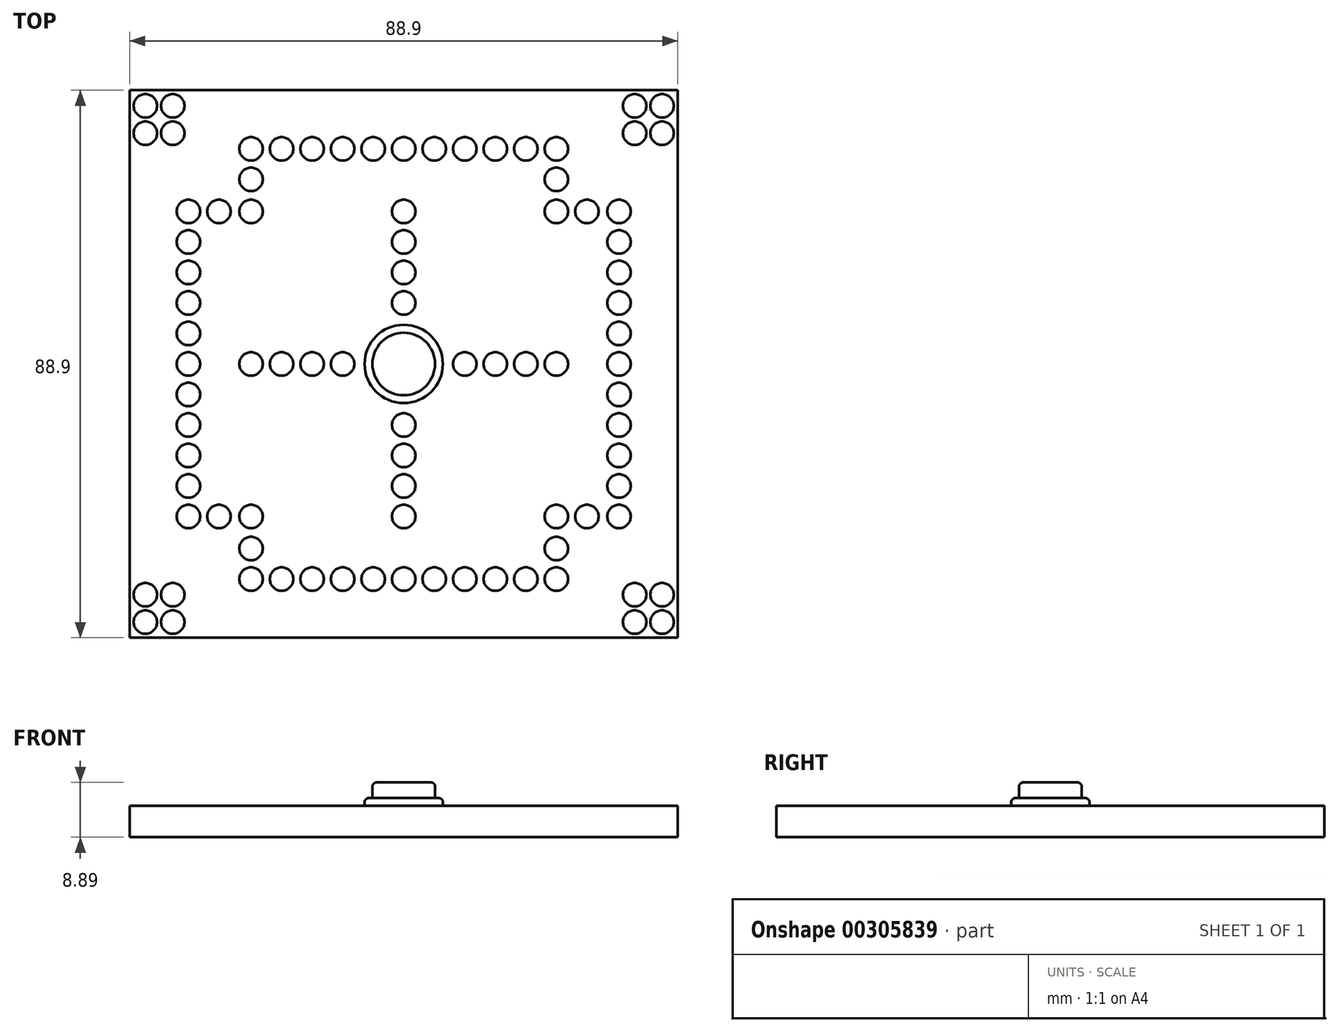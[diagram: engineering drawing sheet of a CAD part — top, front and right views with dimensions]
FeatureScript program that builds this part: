
annotation { "Feature Type Name" : "Feature", "Feature Type Description" : "" }
export const myFeature = defineFeature(function(context is Context, id is Id, definition is map)
    precondition{}
    {
        {
            var Q0;
            Q0=qCreatedBy(makeId("Top.planeOp"),FACE);
            var sketch = newSketch(context, id + "F0", { "sketchPlane" : qUnion([Q0])});
            skLineSegment(sketch, "E0.bottom", {"start": v(-44.45, 44.45) * mm, "end": v(44.45, 44.45) * mm});
            skLineSegment(sketch, "E0.top", {"start": v(-44.45, -44.45) * mm, "end": v(44.45, -44.45) * mm});
            skLineSegment(sketch, "E0.left", {"start": v(-44.45, 44.45) * mm, "end": v(-44.45, -44.45) * mm});
            skLineSegment(sketch, "E0.right", {"start": v(44.45, 44.45) * mm, "end": v(44.45, -44.45) * mm});
            skSolve(sketch);
        }
        {
            var Q0;
            Q0=makeQuery(id+"F0.imprint","IMPRINT",FACE,{"disambiguationData":[TD([[makeQuery(id+"F0.imprint","IMPRINT",EDGE,{"derivedFrom":sQuery(id+"F0.wireOp",EDGE,"E0.bottom")}),-1.0]])]});
            extrude(context, id + "F1", {"entities" : qUnion([Q0]), "depth" : 5.08 * mm});
        }
        {
            var Q0;
            Q0=makeQuery(id+"F1.opExtrude","CAP_FACE",FACE,{"disambiguationData":[OSD([sQuery(id+"F0.wireOp",EDGE,"E0.bottom"),sQuery(id+"F0.wireOp",EDGE,"E0.top"),sQuery(id+"F0.wireOp",EDGE,"E0.left"),sQuery(id+"F0.wireOp",EDGE,"E0.right")])],"isStart":false});
            var sketch = newSketch(context, id + "F2", { "sketchPlane" : qUnion([Q0])});
            skCircle(sketch, "E1", {"center": v(0, 24.77) * mm, "radius": 1.9 * mm});
            skCircle(sketch, "E2", {"center": v(24.77, 0) * mm, "radius": 1.9 * mm});
            skCircle(sketch, "E3", {"center": v(0, -24.77) * mm, "radius": 1.9 * mm});
            skCircle(sketch, "E4", {"center": v(-24.77, 0) * mm, "radius": 1.9 * mm});
            skCircle(sketch, "E5", {"center": v(0, 34.93) * mm, "radius": 1.9 * mm});
            skCircle(sketch, "E6", {"center": v(-24.77, 34.92) * mm, "radius": 1.9 * mm});
            skCircle(sketch, "E7.1.0.0", {"center": v(-19.81, 34.92) * mm, "radius": 1.9 * mm});
            skCircle(sketch, "E7.2.0.0", {"center": v(-14.86, 34.92) * mm, "radius": 1.9 * mm});
            skLineSegment(sketch, "E7.direction1", {"start": v(-24.77, 34.92) * mm, "end": v(-19.81, 34.92) * mm, "construction": true});
            skCircle(sketch, "E8.0.3.0", {"center": v(-9.9, 34.92) * mm, "radius": 1.9 * mm});
            skCircle(sketch, "E8.0.4.0", {"center": v(-4.95, 34.92) * mm, "radius": 1.9 * mm});
            skCircle(sketch, "E9.1.0.0", {"center": v(4.95, 34.93) * mm, "radius": 1.9 * mm});
            skCircle(sketch, "E9.2.0.0", {"center": v(9.9, 34.93) * mm, "radius": 1.9 * mm});
            skCircle(sketch, "E9.3.0.0", {"center": v(14.86, 34.93) * mm, "radius": 1.9 * mm});
            skCircle(sketch, "E9.4.0.0", {"center": v(19.81, 34.93) * mm, "radius": 1.9 * mm});
            skCircle(sketch, "E9.5.0.0", {"center": v(24.77, 34.93) * mm, "radius": 1.9 * mm});
            skLineSegment(sketch, "E9.direction1", {"start": v(0, 34.93) * mm, "end": v(4.95, 34.93) * mm, "construction": true});
            skCircle(sketch, "E10", {"center": v(24.77, 29.97) * mm, "radius": 1.9 * mm});
            skCircle(sketch, "E11", {"center": v(24.77, 24.77) * mm, "radius": 1.9 * mm});
            skCircle(sketch, "E12", {"center": v(-24.77, 24.76) * mm, "radius": 1.9 * mm});
            skCircle(sketch, "E13", {"center": v(-24.77, 29.97) * mm, "radius": 1.9 * mm});
            skCircle(sketch, "E14", {"center": v(24.77, -34.93) * mm, "radius": 1.9 * mm});
            skCircle(sketch, "E15.1.0.0", {"center": v(19.81, -34.93) * mm, "radius": 1.9 * mm});
            skCircle(sketch, "E15.2.0.0", {"center": v(14.86, -34.93) * mm, "radius": 1.9 * mm});
            skCircle(sketch, "E15.3.0.0", {"center": v(9.9, -34.93) * mm, "radius": 1.9 * mm});
            skCircle(sketch, "E15.4.0.0", {"center": v(4.95, -34.93) * mm, "radius": 1.9 * mm});
            skCircle(sketch, "E15.5.0.0", {"center": v(0, -34.93) * mm, "radius": 1.9 * mm});
            skCircle(sketch, "E15.6.0.0", {"center": v(-4.95, -34.93) * mm, "radius": 1.9 * mm});
            skCircle(sketch, "E15.7.0.0", {"center": v(-9.9, -34.93) * mm, "radius": 1.9 * mm});
            skCircle(sketch, "E15.8.0.0", {"center": v(-14.86, -34.93) * mm, "radius": 1.9 * mm});
            skCircle(sketch, "E15.9.0.0", {"center": v(-19.81, -34.93) * mm, "radius": 1.9 * mm});
            skCircle(sketch, "E15.10.0.0", {"center": v(-24.77, -34.93) * mm, "radius": 1.9 * mm});
            skLineSegment(sketch, "E15.direction1", {"start": v(24.77, -34.93) * mm, "end": v(19.81, -34.93) * mm, "construction": true});
            skCircle(sketch, "E16", {"center": v(-24.77, -24.77) * mm, "radius": 1.9 * mm});
            skCircle(sketch, "E17", {"center": v(24.77, -24.77) * mm, "radius": 1.9 * mm});
            skCircle(sketch, "E18", {"center": v(-24.76, -29.97) * mm, "radius": 1.9 * mm});
            skCircle(sketch, "E19", {"center": v(24.77, -29.97) * mm, "radius": 1.9 * mm});
            skCircle(sketch, "E20", {"center": v(-34.92, -24.77) * mm, "radius": 1.9 * mm});
            skCircle(sketch, "E21.0.1.0", {"center": v(-34.92, -19.81) * mm, "radius": 1.9 * mm});
            skCircle(sketch, "E21.0.2.0", {"center": v(-34.92, -14.86) * mm, "radius": 1.9 * mm});
            skCircle(sketch, "E21.0.3.0", {"center": v(-34.92, -9.9) * mm, "radius": 1.9 * mm});
            skCircle(sketch, "E21.0.4.0", {"center": v(-34.92, -4.95) * mm, "radius": 1.9 * mm});
            skCircle(sketch, "E21.0.5.0", {"center": v(-34.92, 0) * mm, "radius": 1.9 * mm});
            skCircle(sketch, "E21.0.6.0", {"center": v(-34.92, 4.95) * mm, "radius": 1.9 * mm});
            skCircle(sketch, "E21.0.7.0", {"center": v(-34.92, 9.9) * mm, "radius": 1.9 * mm});
            skCircle(sketch, "E21.0.8.0", {"center": v(-34.92, 14.86) * mm, "radius": 1.9 * mm});
            skCircle(sketch, "E21.0.9.0", {"center": v(-34.92, 19.81) * mm, "radius": 1.9 * mm});
            skCircle(sketch, "E21.0.10.0", {"center": v(-34.92, 24.77) * mm, "radius": 1.9 * mm});
            skLineSegment(sketch, "E21.direction2", {"start": v(-34.92, -24.77) * mm, "end": v(-34.92, -19.81) * mm, "construction": true});
            skCircle(sketch, "E22", {"center": v(34.93, -24.77) * mm, "radius": 1.9 * mm});
            skCircle(sketch, "E23", {"center": v(29.72, -24.77) * mm, "radius": 1.9 * mm});
            skCircle(sketch, "E24", {"center": v(29.72, 24.77) * mm, "radius": 1.9 * mm});
            skCircle(sketch, "E25", {"center": v(-29.97, -24.77) * mm, "radius": 1.9 * mm});
            skCircle(sketch, "E26", {"center": v(-29.97, 24.76) * mm, "radius": 1.9 * mm});
            skCircle(sketch, "E27.0.1.0", {"center": v(34.93, -19.81) * mm, "radius": 1.9 * mm});
            skCircle(sketch, "E27.0.2.0", {"center": v(34.93, -14.86) * mm, "radius": 1.9 * mm});
            skCircle(sketch, "E27.0.3.0", {"center": v(34.93, -9.9) * mm, "radius": 1.9 * mm});
            skCircle(sketch, "E27.0.4.0", {"center": v(34.93, -4.95) * mm, "radius": 1.9 * mm});
            skCircle(sketch, "E27.0.5.0", {"center": v(34.93, 0) * mm, "radius": 1.9 * mm});
            skCircle(sketch, "E27.0.6.0", {"center": v(34.93, 4.95) * mm, "radius": 1.9 * mm});
            skCircle(sketch, "E27.0.7.0", {"center": v(34.93, 9.9) * mm, "radius": 1.9 * mm});
            skCircle(sketch, "E27.0.8.0", {"center": v(34.93, 14.86) * mm, "radius": 1.9 * mm});
            skCircle(sketch, "E27.0.9.0", {"center": v(34.93, 19.81) * mm, "radius": 1.9 * mm});
            skCircle(sketch, "E27.0.10.0", {"center": v(34.93, 24.77) * mm, "radius": 1.9 * mm});
            skLineSegment(sketch, "E27.direction1", {"start": v(34.93, -24.77) * mm, "end": v(60.33, -24.77) * mm, "construction": true});
            skLineSegment(sketch, "E27.direction2", {"start": v(34.93, -24.77) * mm, "end": v(34.93, -19.81) * mm, "construction": true});
            skCircle(sketch, "E28.1.0.0", {"center": v(-19.81, 0) * mm, "radius": 1.9 * mm});
            skCircle(sketch, "E28.2.0.0", {"center": v(-14.86, 0) * mm, "radius": 1.9 * mm});
            skCircle(sketch, "E28.3.0.0", {"center": v(-9.9, 0) * mm, "radius": 1.9 * mm});
            skLineSegment(sketch, "E28.direction1", {"start": v(-24.77, 0) * mm, "end": v(-19.81, 0) * mm, "construction": true});
            skCircle(sketch, "E29.0.1.0", {"center": v(0, -19.81) * mm, "radius": 1.9 * mm});
            skCircle(sketch, "E29.2.0.0", {"center": v(50.8, -24.77) * mm, "radius": 1.9 * mm});
            skCircle(sketch, "E29.2.1.0", {"center": v(50.8, -19.81) * mm, "radius": 1.9 * mm});
            skLineSegment(sketch, "E29.direction2", {"start": v(0, -24.77) * mm, "end": v(0, -19.81) * mm, "construction": true});
            skCircle(sketch, "E30.0.0.2", {"center": v(0, -14.86) * mm, "radius": 1.9 * mm});
            skCircle(sketch, "E30.0.0.3", {"center": v(0, -9.9) * mm, "radius": 1.9 * mm});
            skCircle(sketch, "E30.0.2.2", {"center": v(50.8, -14.86) * mm, "radius": 1.9 * mm});
            skCircle(sketch, "E30.0.2.3", {"center": v(50.8, -9.9) * mm, "radius": 1.9 * mm});
            skCircle(sketch, "E31.0.1.0", {"center": v(0, 19.81) * mm, "radius": 1.9 * mm});
            skCircle(sketch, "E31.2.0.0", {"center": v(50.8, 24.77) * mm, "radius": 1.9 * mm});
            skCircle(sketch, "E31.2.1.0", {"center": v(50.8, 19.81) * mm, "radius": 1.9 * mm});
            skLineSegment(sketch, "E31.direction2", {"start": v(0, 24.77) * mm, "end": v(0, 19.81) * mm, "construction": true});
            skCircle(sketch, "E32.0.0.2", {"center": v(0, 14.86) * mm, "radius": 1.9 * mm});
            skCircle(sketch, "E32.0.0.3", {"center": v(0, 9.9) * mm, "radius": 1.9 * mm});
            skCircle(sketch, "E32.0.2.2", {"center": v(50.8, 14.86) * mm, "radius": 1.9 * mm});
            skCircle(sketch, "E32.0.2.3", {"center": v(50.8, 9.9) * mm, "radius": 1.9 * mm});
            skCircle(sketch, "E33.1.0.0", {"center": v(19.81, 0) * mm, "radius": 1.9 * mm});
            skCircle(sketch, "E33.2.0.0", {"center": v(14.86, 0) * mm, "radius": 1.9 * mm});
            skCircle(sketch, "E33.3.0.0", {"center": v(9.9, 0) * mm, "radius": 1.9 * mm});
            skLineSegment(sketch, "E33.direction1", {"start": v(24.77, 0) * mm, "end": v(19.81, 0) * mm, "construction": true});
            skSolve(sketch);
        }
        {
            var Q0;
            Q0=makeQuery(id+"F2.imprint","IMPRINT",FACE,{"disambiguationData":[TD([[makeQuery(id+"F2.imprint","IMPRINT",EDGE,{"derivedFrom":sQuery(id+"F2.wireOp",EDGE,"E20")}),1.0]])]});
            var Q1;
            Q1=makeQuery(id+"F2.imprint","IMPRINT",FACE,{"disambiguationData":[TD([[makeQuery(id+"F2.imprint","IMPRINT",EDGE,{"derivedFrom":sQuery(id+"F2.wireOp",EDGE,"E25")}),1.0]])]});
            var Q2;
            Q2=makeQuery(id+"F2.imprint","IMPRINT",FACE,{"disambiguationData":[TD([[makeQuery(id+"F2.imprint","IMPRINT",EDGE,{"derivedFrom":sQuery(id+"F2.wireOp",EDGE,"E16")}),1.0]])]});
            var Q3;
            Q3=makeQuery(id+"F2.imprint","IMPRINT",FACE,{"disambiguationData":[TD([[makeQuery(id+"F2.imprint","IMPRINT",EDGE,{"derivedFrom":sQuery(id+"F2.wireOp",EDGE,"E18")}),1.0]])]});
            var Q4;
            Q4=makeQuery(id+"F2.imprint","IMPRINT",FACE,{"disambiguationData":[TD([[makeQuery(id+"F2.imprint","IMPRINT",EDGE,{"derivedFrom":sQuery(id+"F2.wireOp",EDGE,"E15.10.0.0")}),1.0]])]});
            var Q5;
            Q5=makeQuery(id+"F2.imprint","IMPRINT",FACE,{"disambiguationData":[TD([[makeQuery(id+"F2.imprint","IMPRINT",EDGE,{"derivedFrom":sQuery(id+"F2.wireOp",EDGE,"E15.9.0.0")}),1.0]])]});
            var Q6;
            Q6=makeQuery(id+"F2.imprint","IMPRINT",FACE,{"disambiguationData":[TD([[makeQuery(id+"F2.imprint","IMPRINT",EDGE,{"derivedFrom":sQuery(id+"F2.wireOp",EDGE,"E15.8.0.0")}),1.0]])]});
            var Q7;
            Q7=makeQuery(id+"F2.imprint","IMPRINT",FACE,{"disambiguationData":[TD([[makeQuery(id+"F2.imprint","IMPRINT",EDGE,{"derivedFrom":sQuery(id+"F2.wireOp",EDGE,"E15.7.0.0")}),1.0]])]});
            var Q8;
            Q8=makeQuery(id+"F2.imprint","IMPRINT",FACE,{"disambiguationData":[TD([[makeQuery(id+"F2.imprint","IMPRINT",EDGE,{"derivedFrom":sQuery(id+"F2.wireOp",EDGE,"E15.6.0.0")}),1.0]])]});
            var Q9;
            Q9=makeQuery(id+"F2.imprint","IMPRINT",FACE,{"disambiguationData":[TD([[makeQuery(id+"F2.imprint","IMPRINT",EDGE,{"derivedFrom":sQuery(id+"F2.wireOp",EDGE,"E15.5.0.0")}),1.0]])]});
            var Q10;
            Q10=makeQuery(id+"F2.imprint","IMPRINT",FACE,{"disambiguationData":[TD([[makeQuery(id+"F2.imprint","IMPRINT",EDGE,{"derivedFrom":sQuery(id+"F2.wireOp",EDGE,"E15.4.0.0")}),1.0]])]});
            var Q11;
            Q11=makeQuery(id+"F2.imprint","IMPRINT",FACE,{"disambiguationData":[TD([[makeQuery(id+"F2.imprint","IMPRINT",EDGE,{"derivedFrom":sQuery(id+"F2.wireOp",EDGE,"E15.3.0.0")}),1.0]])]});
            var Q12;
            Q12=makeQuery(id+"F2.imprint","IMPRINT",FACE,{"disambiguationData":[TD([[makeQuery(id+"F2.imprint","IMPRINT",EDGE,{"derivedFrom":sQuery(id+"F2.wireOp",EDGE,"E15.2.0.0")}),1.0]])]});
            var Q13;
            Q13=makeQuery(id+"F2.imprint","IMPRINT",FACE,{"disambiguationData":[TD([[makeQuery(id+"F2.imprint","IMPRINT",EDGE,{"derivedFrom":sQuery(id+"F2.wireOp",EDGE,"E15.1.0.0")}),1.0]])]});
            var Q14;
            Q14=makeQuery(id+"F2.imprint","IMPRINT",FACE,{"disambiguationData":[TD([[makeQuery(id+"F2.imprint","IMPRINT",EDGE,{"derivedFrom":sQuery(id+"F2.wireOp",EDGE,"E14")}),1.0]])]});
            var Q15;
            Q15=makeQuery(id+"F2.imprint","IMPRINT",FACE,{"disambiguationData":[TD([[makeQuery(id+"F2.imprint","IMPRINT",EDGE,{"derivedFrom":sQuery(id+"F2.wireOp",EDGE,"E19")}),1.0]])]});
            var Q16;
            Q16=makeQuery(id+"F2.imprint","IMPRINT",FACE,{"disambiguationData":[TD([[makeQuery(id+"F2.imprint","IMPRINT",EDGE,{"derivedFrom":sQuery(id+"F2.wireOp",EDGE,"E17")}),1.0]])]});
            var Q17;
            Q17=makeQuery(id+"F2.imprint","IMPRINT",FACE,{"disambiguationData":[TD([[makeQuery(id+"F2.imprint","IMPRINT",EDGE,{"derivedFrom":sQuery(id+"F2.wireOp",EDGE,"E23")}),1.0]])]});
            var Q18;
            Q18=makeQuery(id+"F2.imprint","IMPRINT",FACE,{"disambiguationData":[TD([[makeQuery(id+"F2.imprint","IMPRINT",EDGE,{"derivedFrom":sQuery(id+"F2.wireOp",EDGE,"E22")}),1.0]])]});
            var Q19;
            Q19=makeQuery(id+"F2.imprint","IMPRINT",FACE,{"disambiguationData":[TD([[makeQuery(id+"F2.imprint","IMPRINT",EDGE,{"derivedFrom":sQuery(id+"F2.wireOp",EDGE,"E27.0.1.0")}),1.0]])]});
            var Q20;
            Q20=makeQuery(id+"F2.imprint","IMPRINT",FACE,{"disambiguationData":[TD([[makeQuery(id+"F2.imprint","IMPRINT",EDGE,{"derivedFrom":sQuery(id+"F2.wireOp",EDGE,"E27.0.2.0")}),1.0]])]});
            var Q21;
            Q21=makeQuery(id+"F2.imprint","IMPRINT",FACE,{"disambiguationData":[TD([[makeQuery(id+"F2.imprint","IMPRINT",EDGE,{"derivedFrom":sQuery(id+"F2.wireOp",EDGE,"E27.0.3.0")}),1.0]])]});
            var Q22;
            Q22=makeQuery(id+"F2.imprint","IMPRINT",FACE,{"disambiguationData":[TD([[makeQuery(id+"F2.imprint","IMPRINT",EDGE,{"derivedFrom":sQuery(id+"F2.wireOp",EDGE,"E27.0.4.0")}),1.0]])]});
            var Q23;
            Q23=makeQuery(id+"F2.imprint","IMPRINT",FACE,{"disambiguationData":[TD([[makeQuery(id+"F2.imprint","IMPRINT",EDGE,{"derivedFrom":sQuery(id+"F2.wireOp",EDGE,"E27.0.5.0")}),1.0]])]});
            var Q24;
            Q24=makeQuery(id+"F2.imprint","IMPRINT",FACE,{"disambiguationData":[TD([[makeQuery(id+"F2.imprint","IMPRINT",EDGE,{"derivedFrom":sQuery(id+"F2.wireOp",EDGE,"E27.0.6.0")}),1.0]])]});
            var Q25;
            Q25=makeQuery(id+"F2.imprint","IMPRINT",FACE,{"disambiguationData":[TD([[makeQuery(id+"F2.imprint","IMPRINT",EDGE,{"derivedFrom":sQuery(id+"F2.wireOp",EDGE,"E27.0.7.0")}),1.0]])]});
            var Q26;
            Q26=makeQuery(id+"F2.imprint","IMPRINT",FACE,{"disambiguationData":[TD([[makeQuery(id+"F2.imprint","IMPRINT",EDGE,{"derivedFrom":sQuery(id+"F2.wireOp",EDGE,"E27.0.8.0")}),1.0]])]});
            var Q27;
            Q27=makeQuery(id+"F2.imprint","IMPRINT",FACE,{"disambiguationData":[TD([[makeQuery(id+"F2.imprint","IMPRINT",EDGE,{"derivedFrom":sQuery(id+"F2.wireOp",EDGE,"E27.0.9.0")}),1.0]])]});
            var Q28;
            Q28=makeQuery(id+"F2.imprint","IMPRINT",FACE,{"disambiguationData":[TD([[makeQuery(id+"F2.imprint","IMPRINT",EDGE,{"derivedFrom":sQuery(id+"F2.wireOp",EDGE,"E27.0.10.0")}),1.0]])]});
            var Q29;
            Q29=makeQuery(id+"F2.imprint","IMPRINT",FACE,{"disambiguationData":[TD([[makeQuery(id+"F2.imprint","IMPRINT",EDGE,{"derivedFrom":sQuery(id+"F2.wireOp",EDGE,"E24")}),1.0]])]});
            var Q30;
            Q30=makeQuery(id+"F2.imprint","IMPRINT",FACE,{"disambiguationData":[TD([[makeQuery(id+"F2.imprint","IMPRINT",EDGE,{"derivedFrom":sQuery(id+"F2.wireOp",EDGE,"E11")}),1.0]])]});
            var Q31;
            Q31=makeQuery(id+"F2.imprint","IMPRINT",FACE,{"disambiguationData":[TD([[makeQuery(id+"F2.imprint","IMPRINT",EDGE,{"derivedFrom":sQuery(id+"F2.wireOp",EDGE,"E10")}),1.0]])]});
            var Q32;
            Q32=makeQuery(id+"F2.imprint","IMPRINT",FACE,{"disambiguationData":[TD([[makeQuery(id+"F2.imprint","IMPRINT",EDGE,{"derivedFrom":sQuery(id+"F2.wireOp",EDGE,"E9.5.0.0")}),1.0]])]});
            var Q33;
            Q33=makeQuery(id+"F2.imprint","IMPRINT",FACE,{"disambiguationData":[TD([[makeQuery(id+"F2.imprint","IMPRINT",EDGE,{"derivedFrom":sQuery(id+"F2.wireOp",EDGE,"E9.4.0.0")}),1.0]])]});
            var Q34;
            Q34=makeQuery(id+"F2.imprint","IMPRINT",FACE,{"disambiguationData":[TD([[makeQuery(id+"F2.imprint","IMPRINT",EDGE,{"derivedFrom":sQuery(id+"F2.wireOp",EDGE,"E9.3.0.0")}),1.0]])]});
            var Q35;
            Q35=makeQuery(id+"F2.imprint","IMPRINT",FACE,{"disambiguationData":[TD([[makeQuery(id+"F2.imprint","IMPRINT",EDGE,{"derivedFrom":sQuery(id+"F2.wireOp",EDGE,"E9.2.0.0")}),1.0]])]});
            var Q36;
            Q36=makeQuery(id+"F2.imprint","IMPRINT",FACE,{"disambiguationData":[TD([[makeQuery(id+"F2.imprint","IMPRINT",EDGE,{"derivedFrom":sQuery(id+"F2.wireOp",EDGE,"E9.1.0.0")}),1.0]])]});
            var Q37;
            Q37=makeQuery(id+"F2.imprint","IMPRINT",FACE,{"disambiguationData":[TD([[makeQuery(id+"F2.imprint","IMPRINT",EDGE,{"derivedFrom":sQuery(id+"F2.wireOp",EDGE,"E5")}),1.0]])]});
            var Q38;
            Q38=makeQuery(id+"F2.imprint","IMPRINT",FACE,{"disambiguationData":[TD([[makeQuery(id+"F2.imprint","IMPRINT",EDGE,{"derivedFrom":sQuery(id+"F2.wireOp",EDGE,"E8.0.4.0")}),1.0]])]});
            var Q39;
            Q39=makeQuery(id+"F2.imprint","IMPRINT",FACE,{"disambiguationData":[TD([[makeQuery(id+"F2.imprint","IMPRINT",EDGE,{"derivedFrom":sQuery(id+"F2.wireOp",EDGE,"E7.2.0.0")}),1.0]])]});
            var Q40;
            Q40=makeQuery(id+"F2.imprint","IMPRINT",FACE,{"disambiguationData":[TD([[makeQuery(id+"F2.imprint","IMPRINT",EDGE,{"derivedFrom":sQuery(id+"F2.wireOp",EDGE,"E7.1.0.0")}),1.0]])]});
            var Q41;
            Q41=makeQuery(id+"F2.imprint","IMPRINT",FACE,{"disambiguationData":[TD([[makeQuery(id+"F2.imprint","IMPRINT",EDGE,{"derivedFrom":sQuery(id+"F2.wireOp",EDGE,"E8.0.3.0")}),1.0]])]});
            var Q42;
            Q42=makeQuery(id+"F2.imprint","IMPRINT",FACE,{"disambiguationData":[TD([[makeQuery(id+"F2.imprint","IMPRINT",EDGE,{"derivedFrom":sQuery(id+"F2.wireOp",EDGE,"E6")}),1.0]])]});
            var Q43;
            Q43=makeQuery(id+"F2.imprint","IMPRINT",FACE,{"disambiguationData":[TD([[makeQuery(id+"F2.imprint","IMPRINT",EDGE,{"derivedFrom":sQuery(id+"F2.wireOp",EDGE,"E13")}),1.0]])]});
            var Q44;
            Q44=makeQuery(id+"F2.imprint","IMPRINT",FACE,{"disambiguationData":[TD([[makeQuery(id+"F2.imprint","IMPRINT",EDGE,{"derivedFrom":sQuery(id+"F2.wireOp",EDGE,"E12")}),1.0]])]});
            var Q45;
            Q45=makeQuery(id+"F2.imprint","IMPRINT",FACE,{"disambiguationData":[TD([[makeQuery(id+"F2.imprint","IMPRINT",EDGE,{"derivedFrom":sQuery(id+"F2.wireOp",EDGE,"E26")}),1.0]])]});
            var Q46;
            Q46=makeQuery(id+"F2.imprint","IMPRINT",FACE,{"disambiguationData":[TD([[makeQuery(id+"F2.imprint","IMPRINT",EDGE,{"derivedFrom":sQuery(id+"F2.wireOp",EDGE,"E21.0.10.0")}),1.0]])]});
            var Q47;
            Q47=makeQuery(id+"F2.imprint","IMPRINT",FACE,{"disambiguationData":[TD([[makeQuery(id+"F2.imprint","IMPRINT",EDGE,{"derivedFrom":sQuery(id+"F2.wireOp",EDGE,"E21.0.9.0")}),1.0]])]});
            var Q48;
            Q48=makeQuery(id+"F2.imprint","IMPRINT",FACE,{"disambiguationData":[TD([[makeQuery(id+"F2.imprint","IMPRINT",EDGE,{"derivedFrom":sQuery(id+"F2.wireOp",EDGE,"E21.0.8.0")}),1.0]])]});
            var Q49;
            Q49=makeQuery(id+"F2.imprint","IMPRINT",FACE,{"disambiguationData":[TD([[makeQuery(id+"F2.imprint","IMPRINT",EDGE,{"derivedFrom":sQuery(id+"F2.wireOp",EDGE,"E21.0.7.0")}),1.0]])]});
            var Q50;
            Q50=makeQuery(id+"F2.imprint","IMPRINT",FACE,{"disambiguationData":[TD([[makeQuery(id+"F2.imprint","IMPRINT",EDGE,{"derivedFrom":sQuery(id+"F2.wireOp",EDGE,"E21.0.6.0")}),1.0]])]});
            var Q51;
            Q51=makeQuery(id+"F2.imprint","IMPRINT",FACE,{"disambiguationData":[TD([[makeQuery(id+"F2.imprint","IMPRINT",EDGE,{"derivedFrom":sQuery(id+"F2.wireOp",EDGE,"E21.0.5.0")}),1.0]])]});
            var Q52;
            Q52=makeQuery(id+"F2.imprint","IMPRINT",FACE,{"disambiguationData":[TD([[makeQuery(id+"F2.imprint","IMPRINT",EDGE,{"derivedFrom":sQuery(id+"F2.wireOp",EDGE,"E21.0.4.0")}),1.0]])]});
            var Q53;
            Q53=makeQuery(id+"F2.imprint","IMPRINT",FACE,{"disambiguationData":[TD([[makeQuery(id+"F2.imprint","IMPRINT",EDGE,{"derivedFrom":sQuery(id+"F2.wireOp",EDGE,"E21.0.3.0")}),1.0]])]});
            var Q54;
            Q54=makeQuery(id+"F2.imprint","IMPRINT",FACE,{"disambiguationData":[TD([[makeQuery(id+"F2.imprint","IMPRINT",EDGE,{"derivedFrom":sQuery(id+"F2.wireOp",EDGE,"E21.0.2.0")}),1.0]])]});
            var Q55;
            Q55=makeQuery(id+"F2.imprint","IMPRINT",FACE,{"disambiguationData":[TD([[makeQuery(id+"F2.imprint","IMPRINT",EDGE,{"derivedFrom":sQuery(id+"F2.wireOp",EDGE,"E21.0.1.0")}),1.0]])]});
            var Q56;
            Q56=makeQuery(id+"F2.imprint","IMPRINT",FACE,{"disambiguationData":[TD([[makeQuery(id+"F2.imprint","IMPRINT",EDGE,{"derivedFrom":sQuery(id+"F2.wireOp",EDGE,"E4")}),1.0]])]});
            var Q57;
            Q57=makeQuery(id+"F2.imprint","IMPRINT",FACE,{"disambiguationData":[TD([[makeQuery(id+"F2.imprint","IMPRINT",EDGE,{"derivedFrom":sQuery(id+"F2.wireOp",EDGE,"E28.1.0.0")}),1.0]])]});
            var Q58;
            Q58=makeQuery(id+"F2.imprint","IMPRINT",FACE,{"disambiguationData":[TD([[makeQuery(id+"F2.imprint","IMPRINT",EDGE,{"derivedFrom":sQuery(id+"F2.wireOp",EDGE,"E28.2.0.0")}),1.0]])]});
            var Q59;
            Q59=makeQuery(id+"F2.imprint","IMPRINT",FACE,{"disambiguationData":[TD([[makeQuery(id+"F2.imprint","IMPRINT",EDGE,{"derivedFrom":sQuery(id+"F2.wireOp",EDGE,"E28.3.0.0")}),1.0]])]});
            var Q60;
            Q60=makeQuery(id+"F2.imprint","IMPRINT",FACE,{"disambiguationData":[TD([[makeQuery(id+"F2.imprint","IMPRINT",EDGE,{"derivedFrom":sQuery(id+"F2.wireOp",EDGE,"E33.3.0.0")}),1.0]])]});
            var Q61;
            Q61=makeQuery(id+"F2.imprint","IMPRINT",FACE,{"disambiguationData":[TD([[makeQuery(id+"F2.imprint","IMPRINT",EDGE,{"derivedFrom":sQuery(id+"F2.wireOp",EDGE,"E33.2.0.0")}),1.0]])]});
            var Q62;
            Q62=makeQuery(id+"F2.imprint","IMPRINT",FACE,{"disambiguationData":[TD([[makeQuery(id+"F2.imprint","IMPRINT",EDGE,{"derivedFrom":sQuery(id+"F2.wireOp",EDGE,"E33.1.0.0")}),1.0]])]});
            var Q63;
            Q63=makeQuery(id+"F2.imprint","IMPRINT",FACE,{"disambiguationData":[TD([[makeQuery(id+"F2.imprint","IMPRINT",EDGE,{"derivedFrom":sQuery(id+"F2.wireOp",EDGE,"E2")}),1.0]])]});
            var Q64;
            Q64=makeQuery(id+"F2.imprint","IMPRINT",FACE,{"disambiguationData":[TD([[makeQuery(id+"F2.imprint","IMPRINT",EDGE,{"derivedFrom":sQuery(id+"F2.wireOp",EDGE,"E32.0.0.3")}),1.0]])]});
            var Q65;
            Q65=makeQuery(id+"F2.imprint","IMPRINT",FACE,{"disambiguationData":[TD([[makeQuery(id+"F2.imprint","IMPRINT",EDGE,{"derivedFrom":sQuery(id+"F2.wireOp",EDGE,"E32.0.0.2")}),1.0]])]});
            var Q66;
            Q66=makeQuery(id+"F2.imprint","IMPRINT",FACE,{"disambiguationData":[TD([[makeQuery(id+"F2.imprint","IMPRINT",EDGE,{"derivedFrom":sQuery(id+"F2.wireOp",EDGE,"E31.0.1.0")}),1.0]])]});
            var Q67;
            Q67=makeQuery(id+"F2.imprint","IMPRINT",FACE,{"disambiguationData":[TD([[makeQuery(id+"F2.imprint","IMPRINT",EDGE,{"derivedFrom":sQuery(id+"F2.wireOp",EDGE,"E1")}),1.0]])]});
            var Q68;
            Q68=makeQuery(id+"F2.imprint","IMPRINT",FACE,{"disambiguationData":[TD([[makeQuery(id+"F2.imprint","IMPRINT",EDGE,{"derivedFrom":sQuery(id+"F2.wireOp",EDGE,"E30.0.0.3")}),1.0]])]});
            var Q69;
            Q69=makeQuery(id+"F2.imprint","IMPRINT",FACE,{"disambiguationData":[TD([[makeQuery(id+"F2.imprint","IMPRINT",EDGE,{"derivedFrom":sQuery(id+"F2.wireOp",EDGE,"E30.0.0.2")}),1.0]])]});
            var Q70;
            Q70=makeQuery(id+"F2.imprint","IMPRINT",FACE,{"disambiguationData":[TD([[makeQuery(id+"F2.imprint","IMPRINT",EDGE,{"derivedFrom":sQuery(id+"F2.wireOp",EDGE,"E29.0.1.0")}),1.0]])]});
            var Q71;
            Q71=makeQuery(id+"F2.imprint","IMPRINT",FACE,{"disambiguationData":[TD([[makeQuery(id+"F2.imprint","IMPRINT",EDGE,{"derivedFrom":sQuery(id+"F2.wireOp",EDGE,"E3")}),1.0]])]});
            extrude(context, id + "F3", {"entities" : qUnion([Q0, Q1, Q2, Q3, Q4, Q5, Q6, Q7, Q8, Q9, Q10, Q11, Q12, Q13, Q14, Q15, Q16, Q17, Q18, Q19, Q20, Q21, Q22, Q23, Q24, Q25, Q26, Q27, Q28, Q29, Q30, Q31, Q32, Q33, Q34, Q35, Q36, Q37, Q38, Q39, Q40, Q41, Q42, Q43, Q44, Q45, Q46, Q47, Q48, Q49, Q50, Q51, Q52, Q53, Q54, Q55, Q56, Q57, Q58, Q59, Q60, Q61, Q62, Q63, Q64, Q65, Q66, Q67, Q68, Q69, Q70, Q71]), "operationType" : NewBodyOperationType.ADD, "depth" : 0.03 * mm});
        }
        {
            var Q0;
            Q0=makeQuery(id+"F1.opExtrude","CAP_FACE",FACE,{"disambiguationData":[OSD([sQuery(id+"F0.wireOp",EDGE,"E0.bottom"),sQuery(id+"F0.wireOp",EDGE,"E0.top"),sQuery(id+"F0.wireOp",EDGE,"E0.left"),sQuery(id+"F0.wireOp",EDGE,"E0.right")])],"isStart":false});
            var sketch = newSketch(context, id + "F4", { "sketchPlane" : qUnion([Q0])});
            skCircle(sketch, "E34", {"center": v(41.91, 41.91) * mm, "radius": 1.9 * mm});
            skCircle(sketch, "E35", {"center": v(37.47, 41.91) * mm, "radius": 1.9 * mm});
            skCircle(sketch, "E36", {"center": v(41.91, 37.47) * mm, "radius": 1.9 * mm});
            skCircle(sketch, "E37", {"center": v(37.47, 37.47) * mm, "radius": 1.9 * mm});
            skCircle(sketch, "E38", {"center": v(-41.91, 41.91) * mm, "radius": 1.9 * mm});
            skCircle(sketch, "E39.1.0.0", {"center": v(-37.47, 41.91) * mm, "radius": 1.9 * mm});
            skLineSegment(sketch, "E39.direction1", {"start": v(-41.91, 41.91) * mm, "end": v(-37.47, 41.91) * mm, "construction": true});
            skCircle(sketch, "E40", {"center": v(-41.91, 37.47) * mm, "radius": 1.9 * mm});
            skCircle(sketch, "E41.1.0.0", {"center": v(-37.47, 37.47) * mm, "radius": 1.9 * mm});
            skLineSegment(sketch, "E41.direction1", {"start": v(-41.91, 37.47) * mm, "end": v(-37.47, 37.47) * mm, "construction": true});
            skCircle(sketch, "E42", {"center": v(-41.91, -41.91) * mm, "radius": 1.9 * mm});
            skCircle(sketch, "E43", {"center": v(-41.9, -37.47) * mm, "radius": 1.9 * mm});
            skCircle(sketch, "E44.1.0.0", {"center": v(-37.47, -41.91) * mm, "radius": 1.9 * mm});
            skCircle(sketch, "E44.1.0.1", {"center": v(-37.46, -37.47) * mm, "radius": 1.9 * mm});
            skLineSegment(sketch, "E44.direction1", {"start": v(-41.91, -41.91) * mm, "end": v(-37.47, -41.91) * mm, "construction": true});
            skCircle(sketch, "E45", {"center": v(41.91, -41.91) * mm, "radius": 1.9 * mm});
            skCircle(sketch, "E46", {"center": v(41.91, -37.47) * mm, "radius": 1.9 * mm});
            skCircle(sketch, "E47.1.0.0", {"center": v(37.47, -37.47) * mm, "radius": 1.9 * mm});
            skCircle(sketch, "E47.1.0.1", {"center": v(37.47, -41.91) * mm, "radius": 1.9 * mm});
            skLineSegment(sketch, "E47.direction1", {"start": v(41.91, -41.91) * mm, "end": v(37.47, -41.91) * mm, "construction": true});
            skSolve(sketch);
        }
        {
            var Q0;
            Q0=makeQuery(id+"F4.imprint","IMPRINT",FACE,{"disambiguationData":[TD([[makeQuery(id+"F4.imprint","IMPRINT",EDGE,{"derivedFrom":sQuery(id+"F4.wireOp",EDGE,"E38")}),1.0]])]});
            var Q1;
            Q1=makeQuery(id+"F4.imprint","IMPRINT",FACE,{"disambiguationData":[TD([[makeQuery(id+"F4.imprint","IMPRINT",EDGE,{"derivedFrom":sQuery(id+"F4.wireOp",EDGE,"E39.1.0.0")}),1.0]])]});
            var Q2;
            Q2=makeQuery(id+"F4.imprint","IMPRINT",FACE,{"disambiguationData":[TD([[makeQuery(id+"F4.imprint","IMPRINT",EDGE,{"derivedFrom":sQuery(id+"F4.wireOp",EDGE,"E41.1.0.0")}),1.0]])]});
            var Q3;
            Q3=makeQuery(id+"F4.imprint","IMPRINT",FACE,{"disambiguationData":[TD([[makeQuery(id+"F4.imprint","IMPRINT",EDGE,{"derivedFrom":sQuery(id+"F4.wireOp",EDGE,"E40")}),1.0]])]});
            var Q4;
            Q4=makeQuery(id+"F4.imprint","IMPRINT",FACE,{"disambiguationData":[TD([[makeQuery(id+"F4.imprint","IMPRINT",EDGE,{"derivedFrom":sQuery(id+"F4.wireOp",EDGE,"E35")}),1.0]])]});
            var Q5;
            Q5=makeQuery(id+"F4.imprint","IMPRINT",FACE,{"disambiguationData":[TD([[makeQuery(id+"F4.imprint","IMPRINT",EDGE,{"derivedFrom":sQuery(id+"F4.wireOp",EDGE,"E34")}),1.0]])]});
            var Q6;
            Q6=makeQuery(id+"F4.imprint","IMPRINT",FACE,{"disambiguationData":[TD([[makeQuery(id+"F4.imprint","IMPRINT",EDGE,{"derivedFrom":sQuery(id+"F4.wireOp",EDGE,"E36")}),1.0]])]});
            var Q7;
            Q7=makeQuery(id+"F4.imprint","IMPRINT",FACE,{"disambiguationData":[TD([[makeQuery(id+"F4.imprint","IMPRINT",EDGE,{"derivedFrom":sQuery(id+"F4.wireOp",EDGE,"E37")}),1.0]])]});
            var Q8;
            Q8=makeQuery(id+"F4.imprint","IMPRINT",FACE,{"disambiguationData":[TD([[makeQuery(id+"F4.imprint","IMPRINT",EDGE,{"derivedFrom":sQuery(id+"F4.wireOp",EDGE,"E47.1.0.0")}),1.0]])]});
            var Q9;
            Q9=makeQuery(id+"F4.imprint","IMPRINT",FACE,{"disambiguationData":[TD([[makeQuery(id+"F4.imprint","IMPRINT",EDGE,{"derivedFrom":sQuery(id+"F4.wireOp",EDGE,"E46")}),1.0]])]});
            var Q10;
            Q10=makeQuery(id+"F4.imprint","IMPRINT",FACE,{"disambiguationData":[TD([[makeQuery(id+"F4.imprint","IMPRINT",EDGE,{"derivedFrom":sQuery(id+"F4.wireOp",EDGE,"E45")}),1.0]])]});
            var Q11;
            Q11=makeQuery(id+"F4.imprint","IMPRINT",FACE,{"disambiguationData":[TD([[makeQuery(id+"F4.imprint","IMPRINT",EDGE,{"derivedFrom":sQuery(id+"F4.wireOp",EDGE,"E47.1.0.1")}),1.0]])]});
            var Q12;
            Q12=makeQuery(id+"F4.imprint","IMPRINT",FACE,{"disambiguationData":[TD([[makeQuery(id+"F4.imprint","IMPRINT",EDGE,{"derivedFrom":sQuery(id+"F4.wireOp",EDGE,"E44.1.0.0")}),1.0]])]});
            var Q13;
            Q13=makeQuery(id+"F4.imprint","IMPRINT",FACE,{"disambiguationData":[TD([[makeQuery(id+"F4.imprint","IMPRINT",EDGE,{"derivedFrom":sQuery(id+"F4.wireOp",EDGE,"E44.1.0.1")}),1.0]])]});
            var Q14;
            Q14=makeQuery(id+"F4.imprint","IMPRINT",FACE,{"disambiguationData":[TD([[makeQuery(id+"F4.imprint","IMPRINT",EDGE,{"derivedFrom":sQuery(id+"F4.wireOp",EDGE,"E43")}),1.0]])]});
            var Q15;
            Q15=makeQuery(id+"F4.imprint","IMPRINT",FACE,{"disambiguationData":[TD([[makeQuery(id+"F4.imprint","IMPRINT",EDGE,{"derivedFrom":sQuery(id+"F4.wireOp",EDGE,"E42")}),1.0]])]});
            extrude(context, id + "F5", {"entities" : qUnion([Q0, Q1, Q2, Q3, Q4, Q5, Q6, Q7, Q8, Q9, Q10, Q11, Q12, Q13, Q14, Q15]), "operationType" : NewBodyOperationType.ADD, "depth" : 0.03 * mm});
        }
        {
            var Q0;
            Q0=makeQuery(id+"F1.opExtrude","CAP_FACE",FACE,{"disambiguationData":[OSD([sQuery(id+"F0.wireOp",EDGE,"E0.bottom"),sQuery(id+"F0.wireOp",EDGE,"E0.top"),sQuery(id+"F0.wireOp",EDGE,"E0.left"),sQuery(id+"F0.wireOp",EDGE,"E0.right")])],"isStart":false});
            var sketch = newSketch(context, id + "F6", { "sketchPlane" : qUnion([Q0])});
            skCircle(sketch, "E48", {"center": v(0, 0) * mm, "radius": 6.35 * mm});
            skSolve(sketch);
        }
        {
            var Q0;
            Q0=makeQuery(id+"F6.imprint","IMPRINT",FACE,{"disambiguationData":[TD([[makeQuery(id+"F6.imprint","IMPRINT",EDGE,{"derivedFrom":sQuery(id+"F6.wireOp",EDGE,"E48")}),1.0]])]});
            extrude(context, id + "F7", {"entities" : qUnion([Q0]), "operationType" : NewBodyOperationType.ADD, "depth" : 1.27 * mm});
        }
        {
            var Q0;
            Q0=makeQuery(id+"F7.opExtrude","CAP_FACE",FACE,{"disambiguationData":[OSD([sQuery(id+"F6.wireOp",EDGE,"E48")])],"isStart":false});
            var sketch = newSketch(context, id + "F8", { "sketchPlane" : qUnion([Q0])});
            skCircle(sketch, "E49", {"center": v(0, 0) * mm, "radius": 5.08 * mm});
            skSolve(sketch);
        }
        {
            var Q0;
            Q0=makeQuery(id+"F8.imprint","IMPRINT",FACE,{"disambiguationData":[TD([[makeQuery(id+"F8.imprint","IMPRINT",EDGE,{"derivedFrom":sQuery(id+"F8.wireOp",EDGE,"E49")}),1.0]])]});
            extrude(context, id + "F9", {"entities" : qUnion([Q0]), "operationType" : NewBodyOperationType.ADD, "depth" : 2.54 * mm});
        }
        {
            var Q0;
            Q0=makeQuery(id+"F9.opExtrude","CAP_EDGE",EDGE,{"disambiguationData":[OSD([sQuery(id+"F8.wireOp",EDGE,"E49")])],"isStart":false});
            var Q1;
            Q1=makeQuery(id+"F9.opExtrude","CAP_EDGE",EDGE,{"disambiguationData":[OSD([sQuery(id+"F8.wireOp",EDGE,"E49")])],"isStart":true});
            fillet(context, id + "F10", {"entities" : qUnion([Q0, Q1]), "radius" : 0.64 * mm, "tangentPropagation" : true, "allowEdgeOverflow" : false});
        }
        {
            var Q0;
            Q0=makeQuery(id+"F7.opExtrude","CAP_EDGE",EDGE,{"disambiguationData":[OSD([sQuery(id+"F6.wireOp",EDGE,"E48")])],"isStart":false});
            fillet(context, id + "F11", {"entities" : qUnion([Q0]), "radius" : 0.64 * mm, "tangentPropagation" : true, "allowEdgeOverflow" : false});
        }
    });
